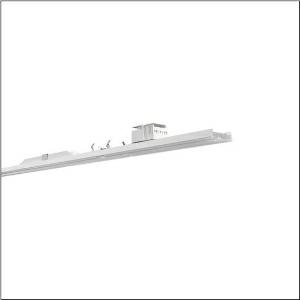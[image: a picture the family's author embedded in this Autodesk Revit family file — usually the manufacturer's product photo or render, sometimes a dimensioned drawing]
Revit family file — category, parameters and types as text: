
# Revit family: licross_r__11_recessed_extreme_mo_51tl18dn485fe_194f
name_source: partatom
category: Lighting Fixtures
units: mm (PartAtom-declared; Revit-internal decimal feet)

## family parameters
Cut with Voids When Loaded = No
Host = Face
Light Source = No
Part Type = Normal
Room Calculation Point = No
Round Connector Dimension = Use Diameter
Shared = No

## types (1)
- --- (1 x LED, 8910 lm, 55.4 W, 4000K)
    Apparent Load = 55 VA
    CIE Flux Codes = 83 96 99 100 100
    Color Rendering = 80
    Color Temperature = 4000K
    Default Elevation = 1800 mm
    Description = Licross® 11 Recessed extreme MOluminaire insert, length: 1.500mm, width: 66mm, height: 67mm, LED rated luminous flux: 8.910lm, light colour: 840, control gear: DALI 2, control gear: ECG DALI, with plug, 5-pole, with phase selection, mains connection: 220..240V, AC, 50/60Hz, halogen-free wiring, primary optical cover: cover, of PMMA, light emission: direct distribution, protection rating (complete): IP40, insulation class (complete): insulation class I (protective earthing), certification: CE, ENEC, VDE, protection symbol: D if used in an environment without relevant dust loads with corresponding accessories, permissible ambient temperature for indoor applications: -25..+50°C, reducing of maximum allowable ambient temperature of 5°C with ceiling mounting, corresponds to IFS (International Featured Standards) requirements for safety and quality in the food industry, packaging unit: 1 piece
    Height = 58 mm
    Lamp = 1 x LED
    Lamp Light Flux = 8910 lm
    Lamp Power = 55.4 W
    Lamp count = 1
    Length = 1500 mm
    Luminous efficacy = 161 lm/W
    Manufacturer = Siteco
    ModVariant = No
    Model = 51TL18DN485FE
    Mounting Place = Ceiling
    Mounting Type = Pendant
    Number of Poles = 1
    OnlyDefault = Yes
    Power Factor = 1
    Product Name = Licross® 11 Recessed extreme MO
    Product group = luminaire insert
    ProductGroupID = 902
    Protection Class = Protection class I
    Protection Degree = IP 40
    RLX_Detail_Level = 1
    RlxData = <blob elided: 22157 chars, md5=1a86d509>
    Socket = socket
    Standby Power = 0 W
    System Light Flux = 8910 lm
    System Power = 55 W
    Type Comments = factory setting: luminous flux: 100 % | dim-lin: 254 | 365 mA
    Type Image = l_1266722.jpg
    URL = http://relux.com
    VarID = @adj_132514
    Voltage = 0 V
    Weight = 0.00 kg
    Width = 66 mm

## geometry (parser evidence)
native form markers: Blend x4, Sweep x10
no freeform markers — native parametric forms only
